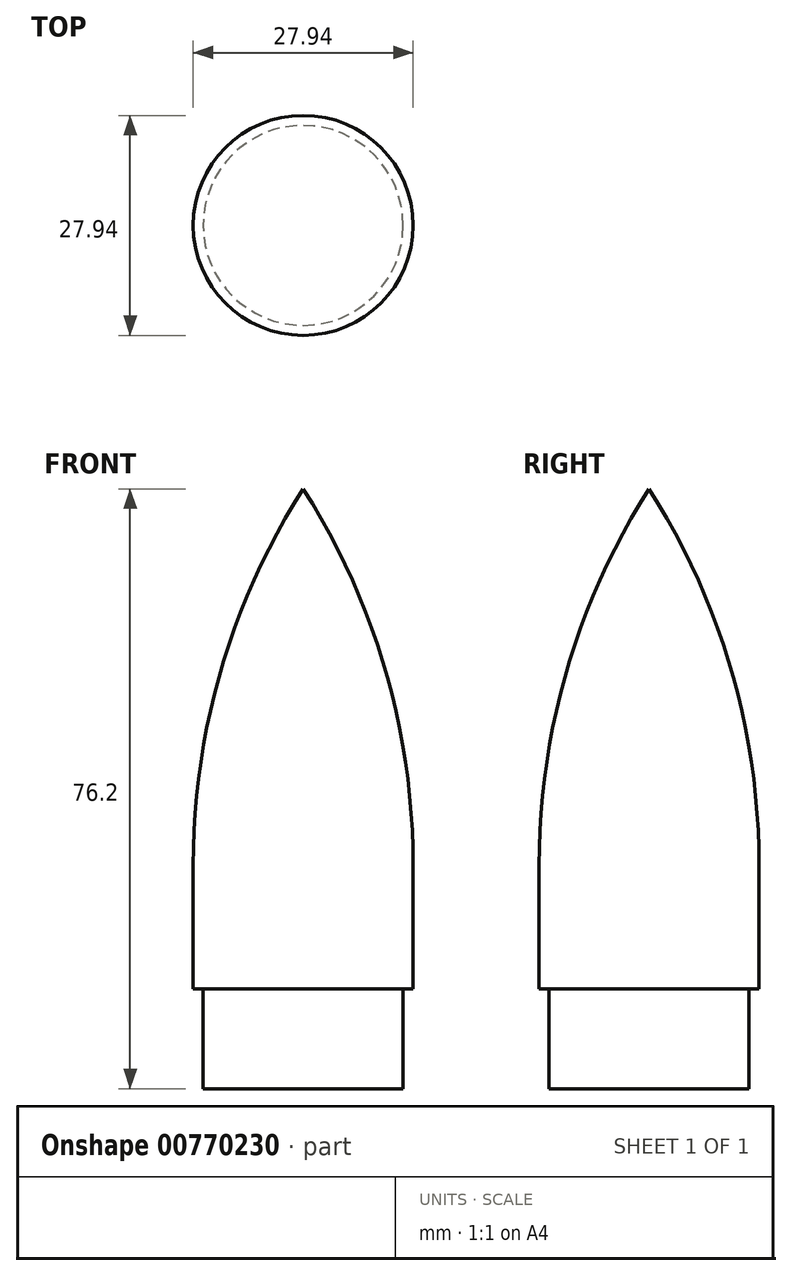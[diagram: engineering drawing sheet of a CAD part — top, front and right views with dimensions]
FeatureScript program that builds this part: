
annotation { "Feature Type Name" : "Feature", "Feature Type Description" : "" }
export const myFeature = defineFeature(function(context is Context, id is Id, definition is map)
    precondition{}
    {
        {
            var Q0;
            Q0=qCreatedBy(makeId("Front.planeOp"),FACE);
            var sketch = newSketch(context, id + "F0", { "sketchPlane" : qUnion([Q0])});
            skArc(sketch, "E0", {"start": v(13.97, 28.41) * mm, "mid": v(10.4, 53.3) * mm, "end": v(0, 76.2) * mm});
            skLineSegment(sketch, "E1", {"start": v(13.97, 28.41) * mm, "end": v(13.97, 12.7) * mm});
            skLineSegment(sketch, "E2", {"start": v(13.97, 12.7) * mm, "end": v(12.7, 12.7) * mm});
            skLineSegment(sketch, "E3", {"start": v(12.7, 12.7) * mm, "end": v(12.7, 0) * mm});
            skLineSegment(sketch, "E4", {"start": v(12.7, 0) * mm, "end": v(0, 0) * mm});
            skLineSegment(sketch, "E5", {"start": v(0, 76.2) * mm, "end": v(0, 0) * mm});
            skLineSegment(sketch, "E6", {"start": v(0, 0) * mm, "end": v(0, -50.7) * mm, "construction": true});
            skSolve(sketch);
        }
        {
            var Q0;
            Q0=makeQuery(id+"F0.imprint","IMPRINT",FACE,{"disambiguationData":[TD([[makeQuery(id+"F0.imprint","IMPRINT",EDGE,{"derivedFrom":sQuery(id+"F0.wireOp",EDGE,"E0")}),1.0]])]});
            var Q1;
            Q1=sQuery(id+"F0.wireOp",EDGE,"E6");
            revolve(context, id + "F1", {"surfaceOperationType" : NewSurfaceOperationType.NEW, "entities" : qUnion([Q0]), "axis" : qUnion([Q1]), "revolveType" : RevolveType.FULL});
        }
    });
